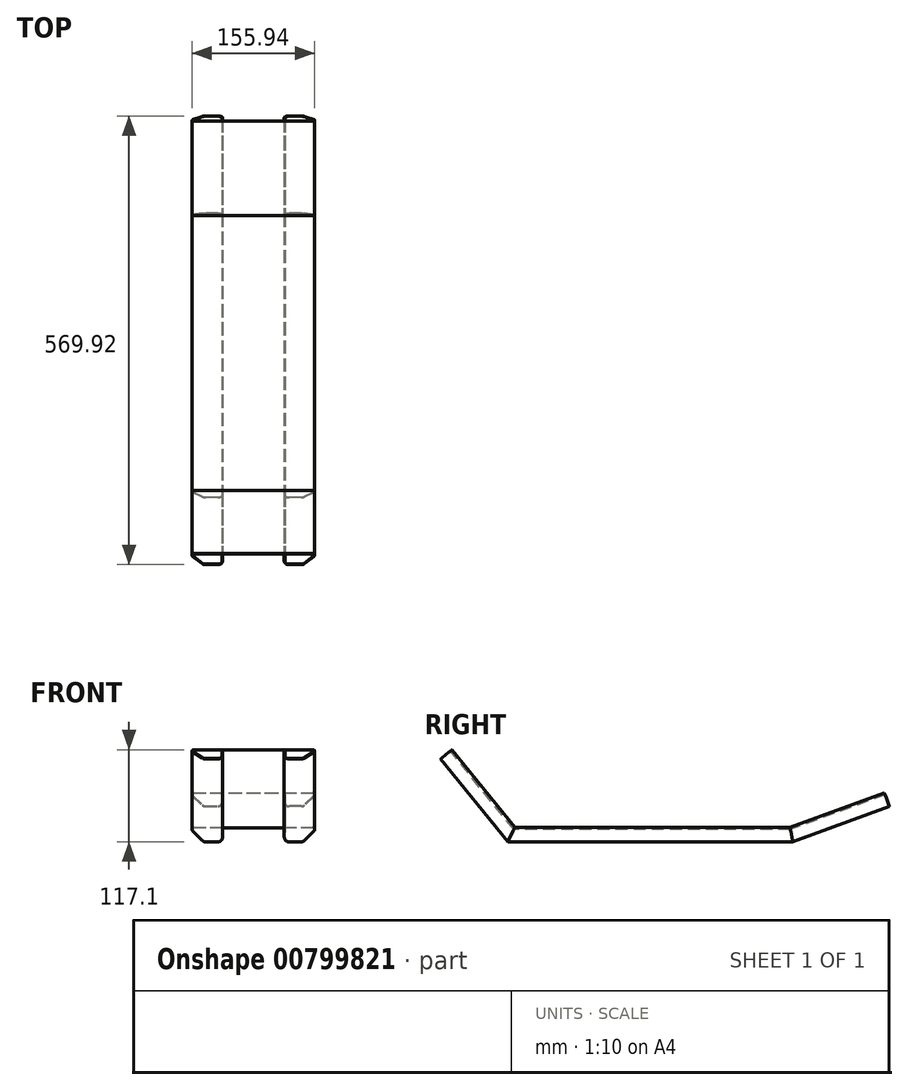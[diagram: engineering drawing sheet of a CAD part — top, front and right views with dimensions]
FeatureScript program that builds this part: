
annotation { "Feature Type Name" : "Feature", "Feature Type Description" : "" }
export const myFeature = defineFeature(function(context is Context, id is Id, definition is map)
    precondition{}
    {
        {
            var Q0;
            Q0=qCreatedBy(makeId("Front.planeOp"),FACE);
            var sketch = newSketch(context, id + "F0", { "sketchPlane" : qUnion([Q0])});
            skLineSegment(sketch, "E0", {"start": v(0, 0) * mm, "end": v(-75.17, 0) * mm});
            skLineSegment(sketch, "E1", {"start": v(-76.59, -3.41) * mm, "end": v(-64.46, -15.54) * mm});
            skLineSegment(sketch, "E2", {"start": v(-60.93, -17) * mm, "end": v(-45, -17) * mm});
            skLineSegment(sketch, "E3", {"start": v(-40, -12) * mm, "end": v(-40, -2) * mm});
            skPoint(sketch, "E4.visualSharp", {"position": v(-40, -17) * mm});
            skArc(sketch, "E4.filletArc", {"start": v(-45, -17) * mm, "mid": v(-41.46, -15.54) * mm, "end": v(-40, -12) * mm});
            skPoint(sketch, "E5.visualSharp", {"position": v(-63, -17) * mm});
            skArc(sketch, "E5.filletArc", {"start": v(-64.46, -15.54) * mm, "mid": v(-62.84, -16.62) * mm, "end": v(-60.93, -17) * mm});
            skPoint(sketch, "E6.visualSharp", {"position": v(-80, 0) * mm});
            skArc(sketch, "E6.filletArc", {"start": v(-75.17, 0) * mm, "mid": v(-77.02, -1.23) * mm, "end": v(-76.59, -3.41) * mm});
            skLineSegment(sketch, "E7.0", {"start": v(-39.2, -12) * mm, "end": v(-39.2, -2) * mm});
            skArc(sketch, "E7.1", {"start": v(-45, -17.8) * mm, "mid": v(-40.9, -16.1) * mm, "end": v(-39.2, -12) * mm});
            skLineSegment(sketch, "E7.2", {"start": v(-60.93, -17.8) * mm, "end": v(-45, -17.8) * mm});
            skLineSegment(sketch, "E7.3", {"start": v(0, 0.8) * mm, "end": v(-75.17, 0.8) * mm});
            skArc(sketch, "E7.4", {"start": v(-75.17, 0.8) * mm, "mid": v(-77.76, -0.93) * mm, "end": v(-77.15, -3.98) * mm});
            skLineSegment(sketch, "E7.5", {"start": v(-77.15, -3.98) * mm, "end": v(-65.03, -16.1) * mm});
            skArc(sketch, "E7.6", {"start": v(-65.03, -16.1) * mm, "mid": v(-63.15, -17.36) * mm, "end": v(-60.93, -17.8) * mm});
            skLineSegment(sketch, "E8", {"start": v(-40, -2) * mm, "end": v(-39.2, -2) * mm});
            skLineSegment(sketch, "E9.MirrorCS", {"start": v(0, 0.8) * mm, "end": v(75.17, 0.8) * mm});
            skLineSegment(sketch, "E10.MirrorCS", {"start": v(0, 0) * mm, "end": v(75.17, 0) * mm});
            skArc(sketch, "E11.MirrorCS", {"start": v(75.17, 0.8) * mm, "mid": v(77.76, -0.93) * mm, "end": v(77.15, -3.98) * mm});
            skArc(sketch, "E12.MirrorCS", {"start": v(75.17, 0) * mm, "mid": v(77.02, -1.23) * mm, "end": v(76.59, -3.41) * mm});
            skLineSegment(sketch, "E13.MirrorCS", {"start": v(76.59, -3.41) * mm, "end": v(64.46, -15.54) * mm});
            skLineSegment(sketch, "E14.MirrorCS", {"start": v(77.15, -3.98) * mm, "end": v(65.03, -16.1) * mm});
            skArc(sketch, "E15.MirrorCS", {"start": v(65.03, -16.1) * mm, "mid": v(63.15, -17.36) * mm, "end": v(60.93, -17.8) * mm});
            skArc(sketch, "E16.MirrorCS", {"start": v(64.46, -15.54) * mm, "mid": v(62.84, -16.62) * mm, "end": v(60.93, -17) * mm});
            skLineSegment(sketch, "E17.MirrorCS", {"start": v(60.93, -17) * mm, "end": v(45, -17) * mm});
            skLineSegment(sketch, "E18.MirrorCS", {"start": v(60.93, -17.8) * mm, "end": v(45, -17.8) * mm});
            skArc(sketch, "E19.MirrorCS", {"start": v(45, -17.8) * mm, "mid": v(40.9, -16.1) * mm, "end": v(39.2, -12) * mm});
            skArc(sketch, "E20.MirrorCS", {"start": v(45, -17) * mm, "mid": v(41.46, -15.54) * mm, "end": v(40, -12) * mm});
            skLineSegment(sketch, "E21.MirrorCS", {"start": v(40, -12) * mm, "end": v(40, -2) * mm});
            skLineSegment(sketch, "E22.MirrorCS", {"start": v(39.2, -12) * mm, "end": v(39.2, -2) * mm});
            skLineSegment(sketch, "E23.MirrorCS", {"start": v(40, -2) * mm, "end": v(39.2, -2) * mm});
            skSolve(sketch);
        }
        {
            var Q0;
            Q0=qCreatedBy(makeId("Right.planeOp"),FACE);
            var sketch = newSketch(context, id + "F1", { "sketchPlane" : qUnion([Q0])});
            skLineSegment(sketch, "E24", {"start": v(0, 0) * mm, "end": v(-150, 0) * mm});
            skLineSegment(sketch, "E25", {"start": v(-150, 0) * mm, "end": v(-230, 98.8) * mm});
            skLineSegment(sketch, "E26", {"start": v(-150, 0) * mm, "end": v(-259.28, 0) * mm, "construction": true});
            skLineSegment(sketch, "E27", {"start": v(0, 0) * mm, "end": v(200, 0) * mm});
            skLineSegment(sketch, "E28", {"start": v(200, 0) * mm, "end": v(320, 43.68) * mm});
            skSolve(sketch);
        }
        {
            var Q0;
            Q0=makeQuery(id+"F0.imprint","IMPRINT",FACE,{"disambiguationData":[TD([[makeQuery(id+"F0.imprint","IMPRINT",EDGE,{"derivedFrom":sQuery(id+"F0.wireOp",EDGE,"E0")}),-1.0]])]});
            var Q1;
            Q1=sQuery(id+"F1.wireOp",EDGE,"E24");
            var Q2;
            Q2=sQuery(id+"F1.wireOp",EDGE,"E25");
            var Q3;
            Q3=sQuery(id+"F1.wireOp",EDGE,"E27");
            var Q4;
            Q4=sQuery(id+"F1.wireOp",EDGE,"64409d0a-ca7a-4195-939c-a6a4c11f636e");
            var Q5;
            Q5=sQuery(id+"F1.wireOp",EDGE,"2k8vtDkk-iuPX-MtkZ-VDfT-JiAgIiBCSSh2");
            var Q6;
            Q6=sQuery(id+"F1.wireOp",EDGE,"E28");
            sweep(context, id + "F2", {"profiles" : qUnion([Q0]), "path" : qUnion([Q1, Q2, Q3, Q4, Q5, Q6])});
        }
    });
